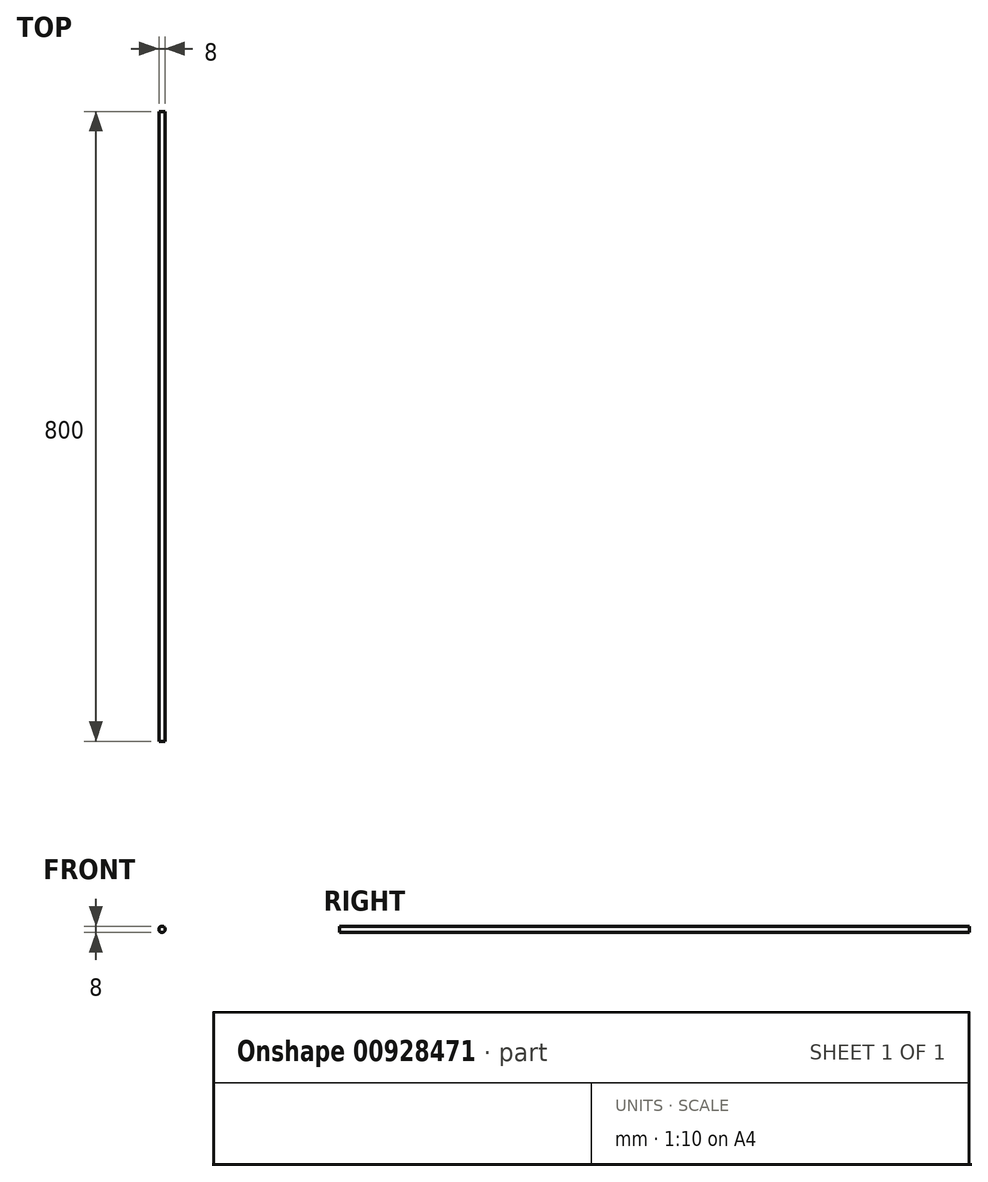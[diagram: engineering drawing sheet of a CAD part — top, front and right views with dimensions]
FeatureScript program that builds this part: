
annotation { "Feature Type Name" : "Feature", "Feature Type Description" : "" }
export const myFeature = defineFeature(function(context is Context, id is Id, definition is map)
    precondition{}
    {
        {
            var Q0;
            Q0=qCreatedBy(makeId("Front.planeOp"),FACE);
            var sketch = newSketch(context, id + "F0", { "sketchPlane" : qUnion([Q0])});
            skCircle(sketch, "E0", {"center": v(0, 0) * mm, "radius": 4 * mm});
            skSolve(sketch);
        }
        {
            var Q0;
            Q0=makeQuery(id+"F0.imprint","IMPRINT",FACE,{"disambiguationData":[TD([[makeQuery(id+"F0.imprint","IMPRINT",EDGE,{"derivedFrom":sQuery(id+"F0.wireOp",EDGE,"E0")}),1.0]])]});
            extrude(context, id + "F1", {"entities" : qUnion([Q0]), "depth" : 800 * mm, "offsetDistance" : 25 * mm});
        }
    });
